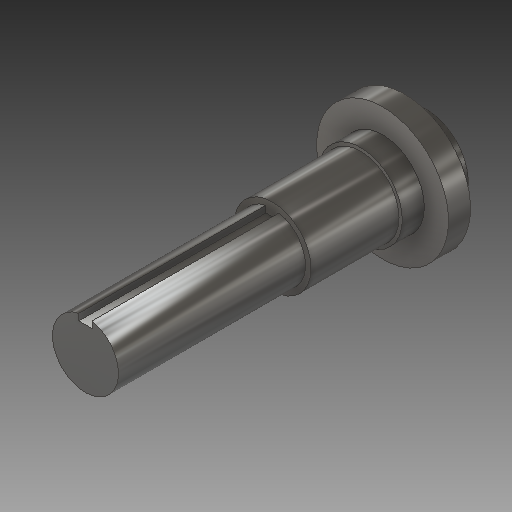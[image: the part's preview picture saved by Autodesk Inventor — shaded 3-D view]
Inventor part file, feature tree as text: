
AUTODESK INVENTOR PART (.ipt)
format: ipt  version: 2019 (Build 230136000, 136)  size: 163,840 bytes
history: native  units: in
note: dims shown in document units (in); Inventor stores cm internally (conversion verified against a paired STEP export)
features: sketch x5, other x3, plane x1
ambient origin geometry x8: Origin, YZ Plane, XZ Plane, XY Plane, X Axis, Y Axis, Z Axis, Center Point
bodies: Solid1 (feature_tree)
feature tree (9):
  other  "project handle part(1)_MIR1.ipt"
  other  "Solid1::project handle part(1)_MIR1.ipt"
  other  "TaggingFeature1"
  sketch  "Sketch1"  dims[d0=0.3937in]
  sketch  "Sketch2"
  sketch  "Sketch3"
  sketch  "Sketch4"
  sketch  "Sketch5"
  plane  "Work Plane1"
